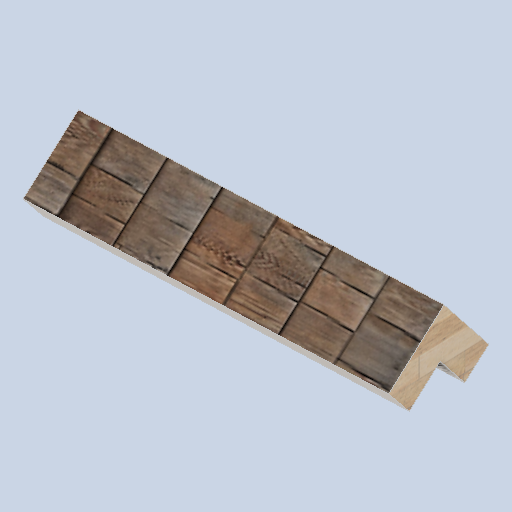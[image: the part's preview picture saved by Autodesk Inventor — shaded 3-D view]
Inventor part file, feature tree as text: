
AUTODESK INVENTOR PART (.ipt)
format: ipt  version: 2024.2 (Build 282272000, 272)  size: 473,088 bytes
history: native  units: mm
features: sketch x9, plane x5, extrude x4, loft x2, projected_geometry x2, other x1
ambient origin geometry x8: Origin, YZ Plane, XZ Plane, XY Plane, X Axis, Y Axis, Z Axis, Center Point
bodies: Solid1 (feature_tree)
feature tree (23):
  sketch  "Sketch1"  dims[d5=0.0mm d6=-8101.0mm d7=800.0mm]
  plane  "Work Plane2"
  loft  "Loft1"
  plane  "Work Plane3"
  extrude  "Extrusion1"  TaperAngle=0.0deg  [1 undecoded]
  sketch  "Sketch5"  dims[d15=6.981317mm d16=0.0mm d17=0.0mm]
  plane  "Work Plane4"
  extrude  "Extrusion2"  TaperAngle=0.0deg  [1 undecoded]
  plane  "Work Plane5"
  sketch  "Sketch7"  dims[d21=0.0mm d22=90.0deg d23=120.0mm]
  sketch  "Sketch8"  dims[d24=120.0mm]
  loft  "Loft2"
  extrude  "Extrusion3"  TaperAngle=0.0deg  [1 undecoded]
  extrude  "Extrusion4"  Depth=120.0mm
  plane  "Work Plane1"
  sketch  "Sketch2"  dims[d8=0.0mm d9=90.0deg d10=0.0mm d11=90.0deg]
  sketch  "Sketch3"  dims[d12=2600.0mm d13=0.0mm d14=0.0mm]
  sketch  "Sketch6"  dims[d18=90.0deg d19=0.0mm d20=90.0deg]
  projected_geometry  "Projected Loop1"
  projected_geometry  "Projected Loop2"
  other  "Edges1"
  sketch  "Sketch9"  dims[d25=100.0mm]
  sketch  "Sketch10"  dims[d26=100.0mm d27=1045.9mm d28=0.0mm d29=2000.0mm d30=0.0mm]
note: 3 required parameter values undecoded (feature->parameter linkage not recoverable at this tier; creation-order binding heuristic only, values carry confidence <= 0.55)
